FCSTD DOCUMENT  (FreeCAD 0.16R6704 (Git))
Label: placa robot
License: All rights reserved
LicenseURL: http://en.wikipedia.org/wiki/All_rights_reserved
objects: Sketcher::SketchObject×1
note: 1 computed .brp shape members not serialized (recipe doc carries the construction recipe); baked Part::Feature solids carry a one-line shape summary decoded from their .brp

FEATURE [Sketcher::SketchObject] Sketch001
  sketch-geometry (17):
    g0: LineSegment StartX=50.5371 StartY=-65.5051 StartZ=0 EndX=75.5371 EndY=-65.5051 EndZ=0
    g1: LineSegment StartX=-50.4721 StartY=-65.5799 StartZ=0 EndX=-75.4721 EndY=-65.5799 EndZ=0
    g2: ArcOfCircle CenterX=0 CenterY=0 CenterZ=0 NormalX=0 NormalY=0 NormalZ=1 Radius=99.9838 StartAngle=3.85697 EndAngle=5.5688
    g3: GeomPoint [constr] X=2.73482e-06 Y=-64.9838 Z=0
    g4: GeomPoint [constr] X=0.000763808 Y=-99.9838 Z=0
    g5: GeomPoint [constr] X=-1.32585e-05 Y=-99.9838 Z=0
    g6: ArcOfCircle CenterX=0 CenterY=0 CenterZ=0 NormalX=0 NormalY=0 NormalZ=1 Radius=112.469 StartAngle=1.10477 EndAngle=2.03618
    g7: LineSegment StartX=50.5371 StartY=100.475 StartZ=0 EndX=50.5371 EndY=7.47531 EndZ=0
    g8: LineSegment StartX=50.5371 StartY=7.47531 StartZ=0 EndX=49.5371 EndY=7.47531 EndZ=0
    g9: LineSegment StartX=49.5371 StartY=7.47531 StartZ=0 EndX=49.5371 EndY=-5.52469 EndZ=0
    g10: LineSegment StartX=49.5371 StartY=-5.52469 StartZ=0 EndX=50.5371 EndY=-5.52469 EndZ=0
    g11: LineSegment StartX=50.5371 StartY=-5.52469 StartZ=0 EndX=50.5371 EndY=-65.5051 EndZ=0
    g12: LineSegment StartX=-50.4721 StartY=100.508 StartZ=0 EndX=-50.4721 EndY=7.50798 EndZ=0
    g13: LineSegment StartX=-50.4721 StartY=-5.49202 StartZ=0 EndX=-49.4721 EndY=-5.49202 EndZ=0
    g14: LineSegment StartX=-50.4721 StartY=7.50798 StartZ=0 EndX=-49.4721 EndY=7.50798 EndZ=0
    g15: LineSegment StartX=-49.4721 StartY=7.50798 StartZ=0 EndX=-49.4721 EndY=-5.49202 EndZ=0
    g16: LineSegment StartX=-50.4721 StartY=-65.5799 StartZ=0 EndX=-50.4721 EndY=-5.49202 EndZ=0
  constraints (40):
    c: Horizontal(g0)
    c: Horizontal(g1)
    c: Coincident(g2,g-1)
    c: Coincident(g2,g1)
    c: Coincident(g0,g2)
    c: Distance(g0) = 25
    c: Distance(g1) = 25
    c: PointOnObject(g4,g2)
    c: PointOnObject(g5,g2)
    c: Coincident(g6,g-1)
    c: Vertical(g7)
    c: Distance(g7,g7) = 93
    c: Distance(g10,g7) = 13
    c: Coincident(g8,g7)
    c: Horizontal(g8)
    c: Distance(g8,g7) = 1
    c: Coincident(g9,g8)
    c: Vertical(g9)
    c: Distance(g9) = 13
    c: Coincident(g10,g9)
    c: Horizontal(g10)
    c: Coincident(g11,g10)
    c: Coincident(g11,g0)
    c: Vertical(g11)
    c: Vertical(g12)
    c: Distance(g6,g12) = 93
    c: Distance(g12,g13) = 13
    c: Horizontal(g13)
    c: Distance(g13,g13) = 1
    c: Coincident(g14,g12)
    c: Horizontal(g14)
    c: Distance(g14,g12) = 1
    c: Coincident(g15,g14)
    c: Coincident(g15,g13)
    c: Vertical(g15)
    c: Coincident(g16,g1)
    c: Vertical(g16)
    c: Coincident(g7,g6)
    c: Coincident(g12,g6)
    c: Coincident(g16,g13)
